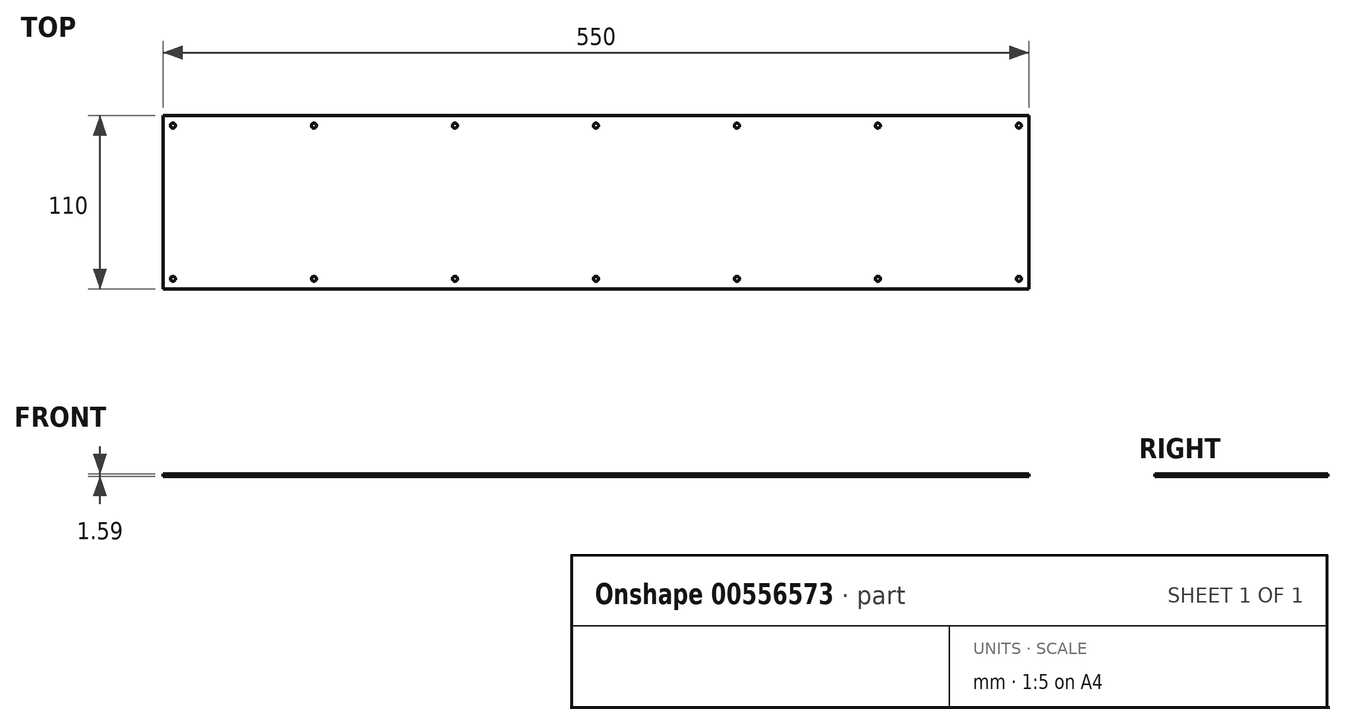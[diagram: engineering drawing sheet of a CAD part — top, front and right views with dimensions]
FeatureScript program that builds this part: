
annotation { "Feature Type Name" : "Feature", "Feature Type Description" : "" }
export const myFeature = defineFeature(function(context is Context, id is Id, definition is map)
    precondition{}
    {
        {
            var Q0;
            Q0=qCreatedBy(makeId("Top.planeOp"),FACE);
            var sketch = newSketch(context, id + "F0", { "sketchPlane" : qUnion([Q0])});
            skLineSegment(sketch, "E0.bottom", {"start": v(-278.36, 62.45) * mm, "end": v(271.64, 62.45) * mm});
            skLineSegment(sketch, "E0.top", {"start": v(-278.36, -47.55) * mm, "end": v(271.64, -47.55) * mm});
            skLineSegment(sketch, "E0.left", {"start": v(-278.36, 62.45) * mm, "end": v(-278.36, -47.55) * mm});
            skLineSegment(sketch, "E0.right", {"start": v(271.64, 62.45) * mm, "end": v(271.64, -47.55) * mm});
            skCircle(sketch, "E1", {"center": v(-272.01, 56.1) * mm, "radius": 1.59 * mm});
            skCircle(sketch, "E2", {"center": v(-272.01, -41.2) * mm, "radius": 1.59 * mm});
            skCircle(sketch, "E3.1.0.0", {"center": v(-182.46, 56.1) * mm, "radius": 1.59 * mm});
            skCircle(sketch, "E3.2.0.0", {"center": v(-92.91, 56.1) * mm, "radius": 1.59 * mm});
            skCircle(sketch, "E3.3.0.0", {"center": v(-3.36, 56.1) * mm, "radius": 1.59 * mm});
            skCircle(sketch, "E3.4.0.0", {"center": v(86.19, 56.1) * mm, "radius": 1.59 * mm});
            skCircle(sketch, "E3.5.0.0", {"center": v(175.74, 56.1) * mm, "radius": 1.59 * mm});
            skCircle(sketch, "E3.6.0.0", {"center": v(265.29, 56.1) * mm, "radius": 1.59 * mm});
            skLineSegment(sketch, "E3.direction1", {"start": v(-272.01, 56.1) * mm, "end": v(-182.46, 56.1) * mm, "construction": true});
            skCircle(sketch, "E4.1.0.0", {"center": v(-182.46, -41.2) * mm, "radius": 1.59 * mm});
            skCircle(sketch, "E4.2.0.0", {"center": v(-92.91, -41.2) * mm, "radius": 1.59 * mm});
            skCircle(sketch, "E4.3.0.0", {"center": v(-3.36, -41.2) * mm, "radius": 1.59 * mm});
            skCircle(sketch, "E4.4.0.0", {"center": v(86.19, -41.2) * mm, "radius": 1.59 * mm});
            skCircle(sketch, "E4.5.0.0", {"center": v(175.74, -41.2) * mm, "radius": 1.59 * mm});
            skCircle(sketch, "E4.6.0.0", {"center": v(265.29, -41.2) * mm, "radius": 1.59 * mm});
            skSolve(sketch);
        }
        {
            var Q0;
            Q0=sQuery(id+"F0.wireOp",EDGE,"E0.bottom");
            var Q1;
            Q1=sQuery(id+"F0.wireOp",EDGE,"E0.top");
            var Q2;
            Q2=sQuery(id+"F0.wireOp",EDGE,"E0.left");
            var Q3;
            Q3=sQuery(id+"F0.wireOp",EDGE,"E0.right");
            var Q4;
            Q4=sQuery(id+"F0.wireOp",EDGE,"E4.3.0.0");
            var Q5;
            Q5=sQuery(id+"F0.wireOp",EDGE,"E4.2.0.0");
            var Q6;
            Q6=sQuery(id+"F0.wireOp",EDGE,"E4.5.0.0");
            var Q7;
            Q7=sQuery(id+"F0.wireOp",EDGE,"E4.1.0.0");
            var Q8;
            Q8=sQuery(id+"F0.wireOp",EDGE,"E4.4.0.0");
            var Q9;
            Q9=sQuery(id+"F0.wireOp",EDGE,"E3.2.0.0");
            var Q10;
            Q10=sQuery(id+"F0.wireOp",EDGE,"E3.3.0.0");
            var Q11;
            Q11=sQuery(id+"F0.wireOp",EDGE,"E3.4.0.0");
            var Q12;
            Q12=sQuery(id+"F0.wireOp",EDGE,"E3.5.0.0");
            var Q13;
            Q13=sQuery(id+"F0.wireOp",EDGE,"E4.6.0.0");
            var Q14;
            Q14=sQuery(id+"F0.wireOp",EDGE,"E2");
            var Q15;
            Q15=sQuery(id+"F0.wireOp",EDGE,"E3.1.0.0");
            var Q16;
            Q16=sQuery(id+"F0.wireOp",EDGE,"E3.6.0.0");
            var Q17;
            Q17=sQuery(id+"F0.wireOp",EDGE,"E1");
            extrude(context, id + "F1", {"bodyType" : ExtendedToolBodyType.SURFACE, "surfaceEntities" : qUnion([Q0, Q1, Q2, Q3, Q4, Q5, Q6, Q7, Q8, Q9, Q10, Q11, Q12, Q13, Q14, Q15, Q16, Q17]), "depth" : 1.59 * mm, "offsetDistance" : 25 * mm});
        }
    });
